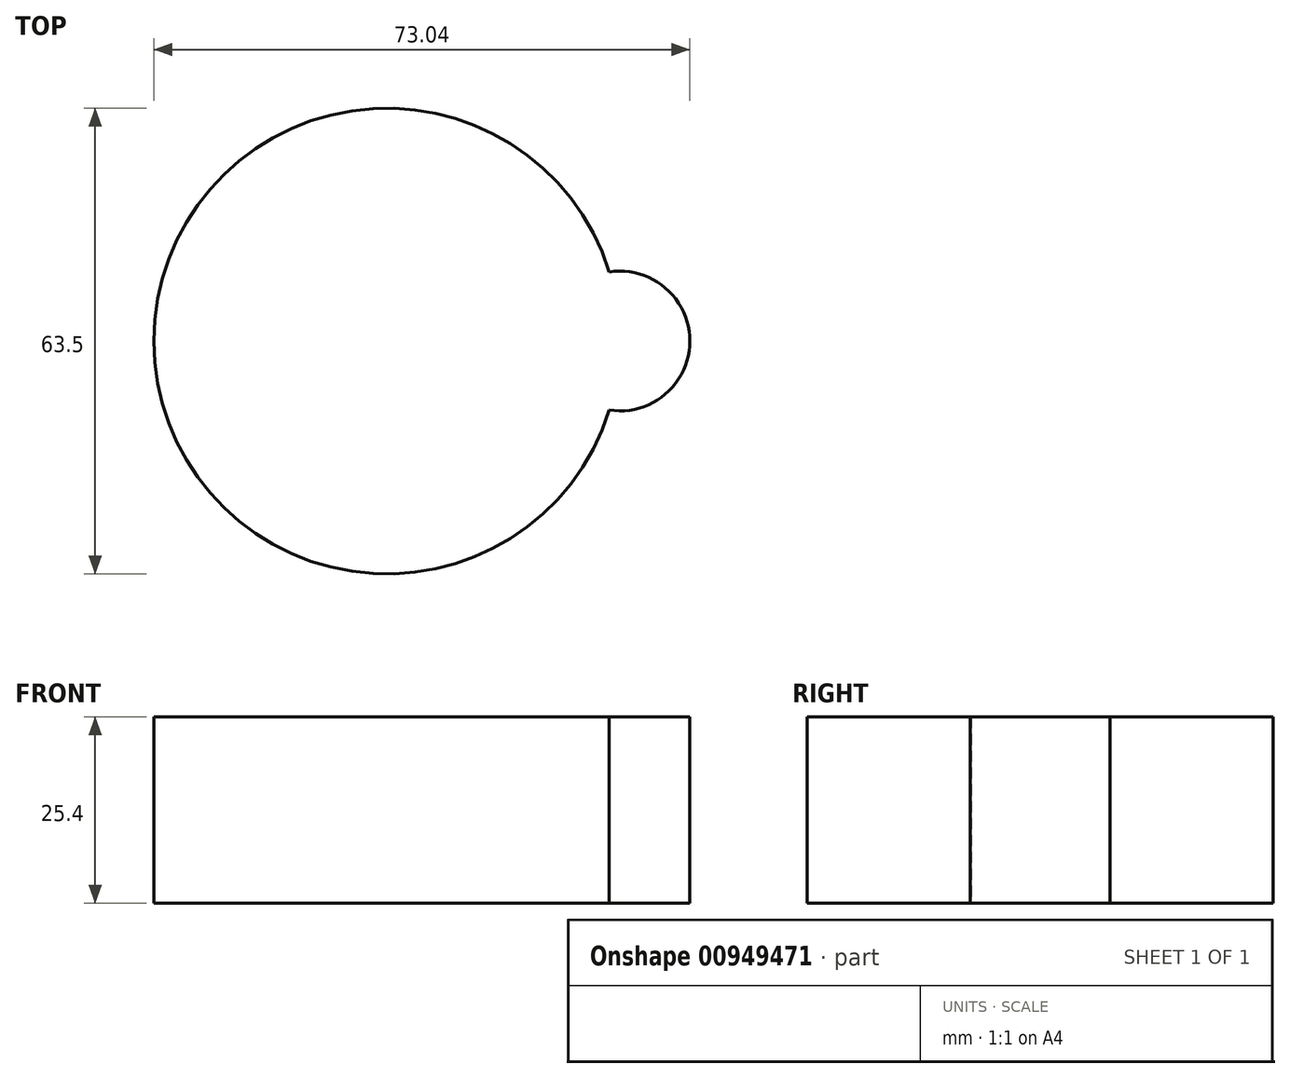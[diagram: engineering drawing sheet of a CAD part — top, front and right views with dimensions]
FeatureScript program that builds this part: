
annotation { "Feature Type Name" : "Feature", "Feature Type Description" : "" }
export const myFeature = defineFeature(function(context is Context, id is Id, definition is map)
    precondition{}
    {
        {
            var Q0;
            Q0=qCreatedBy(makeId("Top.planeOp"),FACE);
            var sketch = newSketch(context, id + "F0", { "sketchPlane" : qUnion([Q0])});
            skCircle(sketch, "E0", {"center": v(0, 0) * mm, "radius": 31.75 * mm});
            skSolve(sketch);
        }
        {
            var Q0;
            Q0=qCreatedBy(makeId("Top.planeOp"),FACE);
            var sketch = newSketch(context, id + "F1", { "sketchPlane" : qUnion([Q0])});
            skCircle(sketch, "E1", {"center": v(31.76, 0) * mm, "radius": 9.53 * mm});
            skCircle(sketch, "E2.1.0", {"center": v(15.88, 27.5) * mm, "radius": 9.53 * mm});
            skCircle(sketch, "E2.2.0", {"center": v(-15.88, 27.5) * mm, "radius": 9.53 * mm});
            skCircle(sketch, "E2.3.0", {"center": v(-31.76, 0) * mm, "radius": 9.53 * mm});
            skCircle(sketch, "E2.4.0", {"center": v(-15.88, -27.5) * mm, "radius": 9.53 * mm});
            skCircle(sketch, "E2.5.0", {"center": v(15.88, -27.5) * mm, "radius": 9.53 * mm});
            skPoint(sketch, "E2.center", {"position": v(0, 0) * mm});
            skSolve(sketch);
        }
        {
            var Q0;
            Q0=makeQuery(id+"F0.imprint","IMPRINT",FACE,{"disambiguationData":[TD([[makeQuery(id+"F0.imprint","IMPRINT",EDGE,{"derivedFrom":sQuery(id+"F0.wireOp",EDGE,"E0")}),1.0]])]});
            extrude(context, id + "F2", {"entities" : qUnion([Q0]), "depth" : 25.4 * mm, "offsetDistance" : 25.4 * mm});
        }
        {
            var Q0;
            Q0=makeQuery(id+"F1.imprint","IMPRINT",FACE,{"disambiguationData":[TD([[makeQuery(id+"F1.imprint","IMPRINT",EDGE,{"derivedFrom":sQuery(id+"F1.wireOp",EDGE,"E1")}),1.0]])]});
            extrude(context, id + "F3", {"entities" : qUnion([Q0]), "operationType" : NewBodyOperationType.ADD, "depth" : 25.4 * mm, "offsetDistance" : 25.4 * mm});
        }
    });
